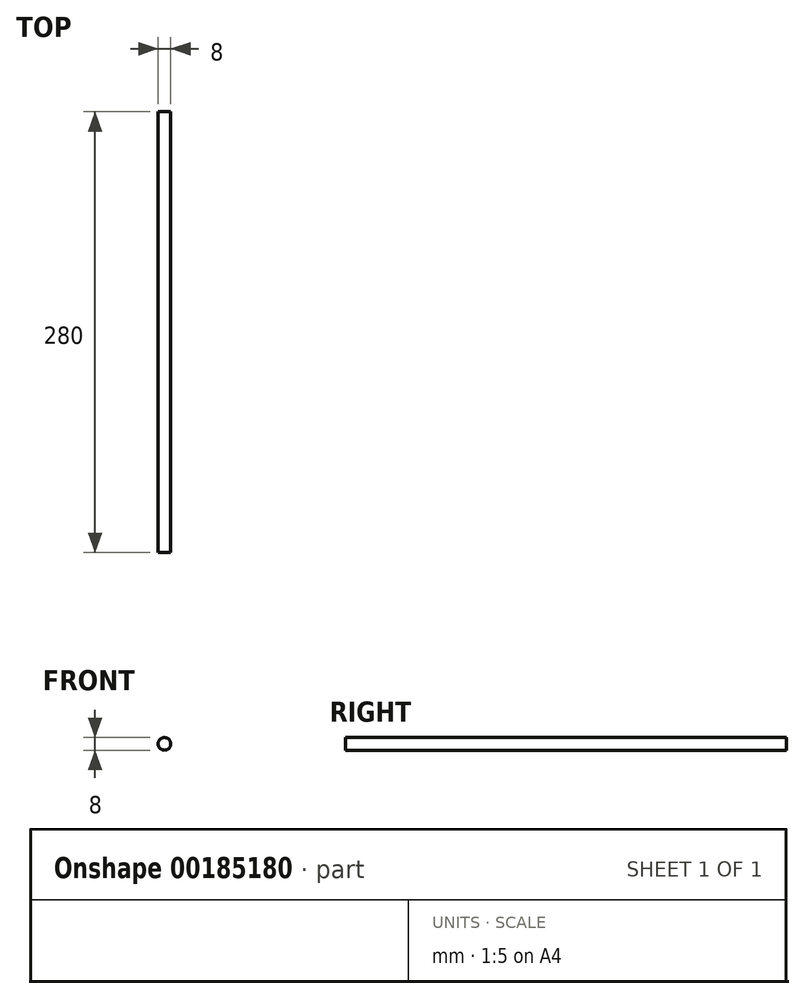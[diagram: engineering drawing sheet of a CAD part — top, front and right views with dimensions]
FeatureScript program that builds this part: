
annotation { "Feature Type Name" : "Feature", "Feature Type Description" : "" }
export const myFeature = defineFeature(function(context is Context, id is Id, definition is map)
    precondition{}
    {
        {
            var Q0;
            Q0=qCreatedBy(makeId("Front.planeOp"),FACE);
            var sketch = newSketch(context, id + "F0", { "sketchPlane" : qUnion([Q0])});
            skCircle(sketch, "E0", {"center": v(0, 0) * mm, "radius": 4 * mm});
            skSolve(sketch);
        }
        {
            var Q0;
            Q0=makeQuery(id+"F0.imprint","IMPRINT",FACE,{"disambiguationData":[TD([[makeQuery(id+"F0.imprint","IMPRINT",EDGE,{"derivedFrom":sQuery(id+"F0.wireOp",EDGE,"E0")}),1.0]])]});
            extrude(context, id + "F1", {"entities" : qUnion([Q0]), "depth" : 280 * mm});
        }
    });
